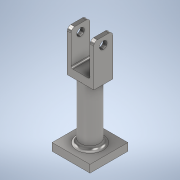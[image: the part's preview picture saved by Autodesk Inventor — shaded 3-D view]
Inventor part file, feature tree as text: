
AUTODESK INVENTOR PART (.ipt)
format: ipt  version: 2022 (Build 260153000, 153)  size: 187,904 bytes
history: native  units: in
note: dims shown in document units (in); Inventor stores cm internally (conversion verified against a paired STEP export)
features: extrude x6, sketch x6, fillet x3
ambient origin geometry x8: Origin, YZ Plane, XZ Plane, XY Plane, X Axis, Y Axis, Z Axis, Center Point
bodies: Solid1 (feature_tree)
feature tree (15):
  extrude  "Extrusion1"  Depth=3.937in
  extrude  "Extrusion2"  Depth=0.7874in TaperAngle=0.0deg
  extrude  "Extrusion3"  Depth=5.9055in TaperAngle=0.0deg
  extrude  "Extrusion4"  Depth=1.378in
  sketch  "Sketch5"  dims[d13=1.378in d14=0.3937in]
  extrude  "Extrusion5"  Depth=0.3937in
  extrude  "Extrusion6"  Depth=3.5433in TaperAngle=0.0deg
  fillet  "Fillet1"  Radius=0.7874in
  fillet  "Fillet2"  Radius=0.7874in
  fillet  "Fillet3"  Radius=0.3937in
  sketch  "Sketch1"  dims[d0=3.937in d1=3.937in]
  sketch  "Sketch2"  dims[d2=3.937in d3=0.7874in d4=0.0in]
  sketch  "Sketch3"  dims[d5=1.9685in d6=5.9055in d7=0.0in]
  sketch  "Sketch4"  dims[d10=0.7874in d11=0.0in d12=1.378in]
  sketch  "Sketch6"  dims[d15=0.3937in d16=3.5433in d17=0.0in d20=0.7874in d23=0.7874in d24=0.3937in d25=0.0in d26=0.3937in d27=0.0in d28=0.1969in d29=0.3937in d30=0.3937in]
